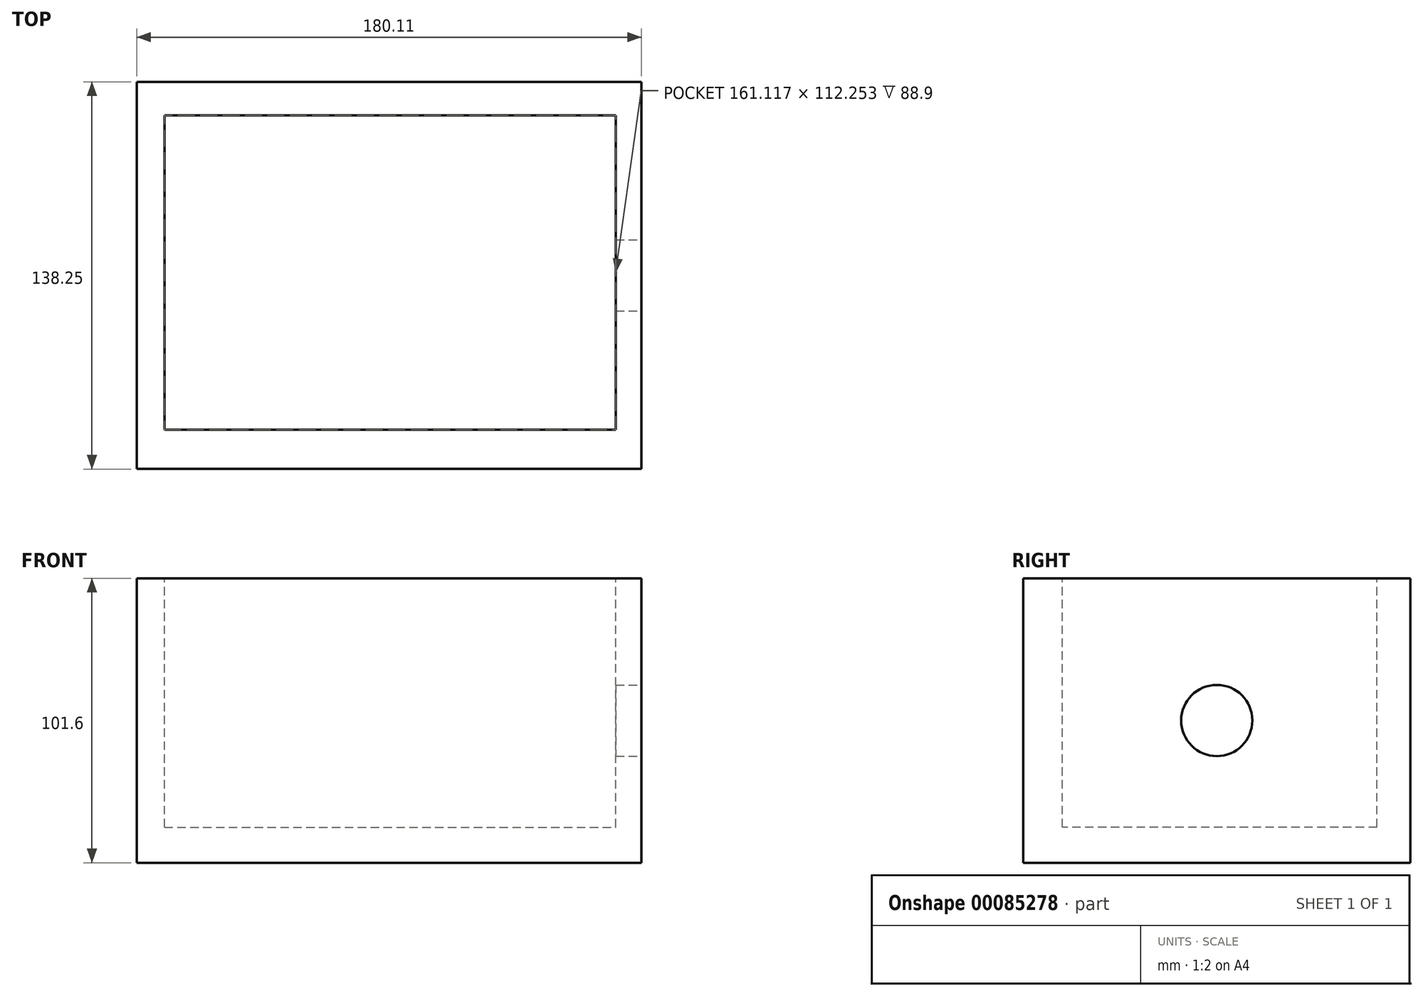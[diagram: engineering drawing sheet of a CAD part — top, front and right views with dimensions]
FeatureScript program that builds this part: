
annotation { "Feature Type Name" : "Feature", "Feature Type Description" : "" }
export const myFeature = defineFeature(function(context is Context, id is Id, definition is map)
    precondition{}
    {
        {
            var Q0;
            Q0=qCreatedBy(makeId("Top.planeOp"),FACE);
            var sketch = newSketch(context, id + "F0", { "sketchPlane" : qUnion([Q0])});
            skLineSegment(sketch, "E0.bottom", {"start": v(-118.18, 69.72) * mm, "end": v(61.93, 69.72) * mm});
            skLineSegment(sketch, "E0.top", {"start": v(-118.18, -68.53) * mm, "end": v(61.93, -68.53) * mm});
            skLineSegment(sketch, "E0.left", {"start": v(-118.18, 69.72) * mm, "end": v(-118.18, -68.53) * mm});
            skLineSegment(sketch, "E0.right", {"start": v(61.93, 69.72) * mm, "end": v(61.93, -68.53) * mm});
            skSolve(sketch);
        }
        {
            var Q0;
            Q0=makeQuery(id+"F0.imprint","IMPRINT",FACE,{"disambiguationData":[TD([[makeQuery(id+"F0.imprint","IMPRINT",EDGE,{"derivedFrom":sQuery(id+"F0.wireOp",EDGE,"E0.bottom")}),-1.0]])]});
            extrude(context, id + "F1", {"entities" : qUnion([Q0]), "depth" : 101.6 * mm});
        }
        {
            var Q0;
            Q0=makeQuery(id+"F1.opExtrude","CAP_FACE",FACE,{"disambiguationData":[OSD([sQuery(id+"F0.wireOp",EDGE,"E0.bottom"),sQuery(id+"F0.wireOp",EDGE,"E0.top"),sQuery(id+"F0.wireOp",EDGE,"E0.left"),sQuery(id+"F0.wireOp",EDGE,"E0.right")])],"isStart":false});
            var sketch = newSketch(context, id + "F2", { "sketchPlane" : qUnion([Q0])});
            skLineSegment(sketch, "E1.bottom", {"start": v(-108.29, 57.79) * mm, "end": v(52.83, 57.79) * mm});
            skLineSegment(sketch, "E1.top", {"start": v(-108.29, -54.47) * mm, "end": v(52.83, -54.47) * mm});
            skLineSegment(sketch, "E1.left", {"start": v(-108.29, 57.79) * mm, "end": v(-108.29, -54.47) * mm});
            skLineSegment(sketch, "E1.right", {"start": v(52.83, 57.79) * mm, "end": v(52.83, -54.47) * mm});
            skSolve(sketch);
        }
        {
            var Q0;
            Q0=makeQuery(id+"F2.imprint","IMPRINT",FACE,{"disambiguationData":[TD([[makeQuery(id+"F2.imprint","IMPRINT",EDGE,{"derivedFrom":sQuery(id+"F2.wireOp",EDGE,"E1.bottom")}),-1.0]])]});
            extrude(context, id + "F3", {"entities" : qUnion([Q0]), "operationType" : NewBodyOperationType.REMOVE, "oppositeDirection" : true, "depth" : 88.9 * mm});
        }
        {
            var Q0;
            Q0=makeQuery(id+"F1.opExtrude","SWEPT_FACE",FACE,{"disambiguationData":[OSD([sQuery(id+"F0.wireOp",EDGE,"E0.right")])]});
            var sketch = newSketch(context, id + "F4", { "sketchPlane" : qUnion([Q0])});
            skCircle(sketch, "E2", {"center": v(0.6, 50.8) * mm, "radius": 12.7 * mm});
            skPoint(sketch, "E2.centerSnap0", {"position": v(-68.53, 50.8) * mm});
            skPoint(sketch, "E2.centerSnap1", {"position": v(0.6, 101.6) * mm});
            skSolve(sketch);
        }
        {
            var Q0;
            Q0=makeQuery(id+"F4.imprint","IMPRINT",FACE,{"disambiguationData":[TD([[makeQuery(id+"F4.imprint","IMPRINT",EDGE,{"derivedFrom":sQuery(id+"F4.wireOp",EDGE,"E2")}),1.0]])]});
            extrude(context, id + "F5", {"entities" : qUnion([Q0]), "operationType" : NewBodyOperationType.REMOVE, "endBound" : BoundingType.UP_TO_NEXT, "oppositeDirection" : true, "depth" : 25.4 * mm});
        }
    });
